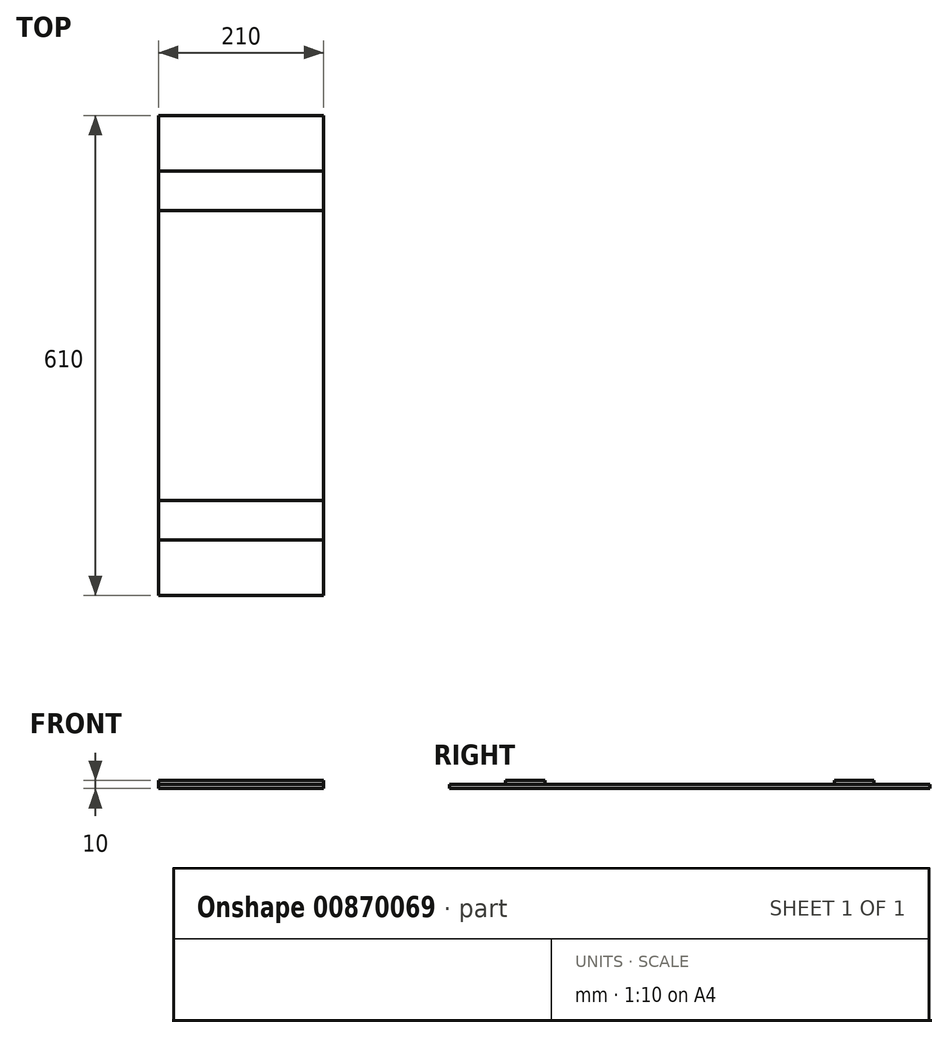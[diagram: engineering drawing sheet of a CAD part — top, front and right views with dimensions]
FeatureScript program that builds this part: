
annotation { "Feature Type Name" : "Feature", "Feature Type Description" : "" }
export const myFeature = defineFeature(function(context is Context, id is Id, definition is map)
    precondition{}
    {
        {
            assignVariable(context, id + "F0", {"name" : "width", "anyValue" : 5});
        }
        {
            var Q0;
            Q0=qCreatedBy(makeId("Top.planeOp"),FACE);
            var sketch = newSketch(context, id + "F1", { "sketchPlane" : qUnion([Q0])});
            skLineSegment(sketch, "E0.bottom", {"start": v(105, 305) * mm, "end": v(-105, 305) * mm});
            skLineSegment(sketch, "E0.top", {"start": v(105, -305) * mm, "end": v(-105, -305) * mm});
            skLineSegment(sketch, "E0.left", {"start": v(105, 305) * mm, "end": v(105, -305) * mm});
            skLineSegment(sketch, "E0.right", {"start": v(-105, 305) * mm, "end": v(-105, -305) * mm});
            skPoint(sketch, "E0.middle", {"position": v(0, 0) * mm});
            skSolve(sketch);
        }
        {
            var Q0;
            Q0 = qSketchRegion(id + "F1", true);
            extrude(context, id + "F2", {"entities" : qUnion([Q0]), "depth" : (getVariable(context, 'width')) * mm, "offsetDistance" : 25 * mm});
        }
        {
            var Q0;
            Q0=makeQuery(id+"F2.opExtrude","CAP_FACE",FACE,{"disambiguationData":[OSD([sQuery(id+"F1.wireOp",EDGE,"E0.bottom"),sQuery(id+"F1.wireOp",EDGE,"E0.top"),sQuery(id+"F1.wireOp",EDGE,"E0.left"),sQuery(id+"F1.wireOp",EDGE,"E0.right")])],"isStart":false});
            var sketch = newSketch(context, id + "F3", { "sketchPlane" : qUnion([Q0])});
            skLineSegment(sketch, "E1.bottom", {"start": v(-105, -184) * mm, "end": v(105, -184) * mm});
            skLineSegment(sketch, "E1.top", {"start": v(-105, -234) * mm, "end": v(105, -234) * mm});
            skLineSegment(sketch, "E1.left", {"start": v(-105, -184) * mm, "end": v(-105, -234) * mm});
            skLineSegment(sketch, "E1.right", {"start": v(105, -184) * mm, "end": v(105, -234) * mm});
            skPoint(sketch, "E1.middle", {"position": v(0, -209) * mm});
            skPoint(sketch, "E1.middle.positionSnap0", {"position": v(0, -305) * mm});
            skPoint(sketch, "E1.centerSnap0", {"position": v(0, -305) * mm});
            skLineSegment(sketch, "E2.MirrorCS", {"start": v(-105, 184) * mm, "end": v(-105, 234) * mm});
            skLineSegment(sketch, "E3.MirrorCS", {"start": v(105, 184) * mm, "end": v(105, 234) * mm});
            skLineSegment(sketch, "E4.MirrorCS", {"start": v(-105, 234) * mm, "end": v(105, 234) * mm});
            skLineSegment(sketch, "E5.MirrorCS", {"start": v(-105, 184) * mm, "end": v(105, 184) * mm});
            skPoint(sketch, "E6.MirrorP", {"position": v(0, 209) * mm});
            skSolve(sketch);
        }
        {
            var Q0;
            Q0=makeQuery(id+"F3.imprint","IMPRINT",FACE,{"disambiguationData":[TD([[makeQuery(id+"F3.imprint","IMPRINT",EDGE,{"derivedFrom":sQuery(id+"F3.wireOp",EDGE,"E1.bottom")}),-1.0]])]});
            var Q1;
            Q1=makeQuery(id+"F3.imprint","IMPRINT",FACE,{"disambiguationData":[TD([[makeQuery(id+"F3.imprint","IMPRINT",EDGE,{"derivedFrom":sQuery(id+"F3.wireOp",EDGE,"E2.MirrorCS")}),1.0]])]});
            extrude(context, id + "F4", {"entities" : qUnion([Q0, Q1]), "depth" : (getVariable(context, 'width')) * mm, "offsetDistance" : 25 * mm});
        }
    });
